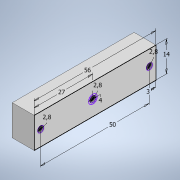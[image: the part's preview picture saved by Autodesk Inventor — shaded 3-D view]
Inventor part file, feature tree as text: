
AUTODESK INVENTOR PART (.ipt)
format: ipt  version: 2020.3 (Build 243373000, 373)  size: 239,616 bytes
history: native  units: mm
features: extrude x2, sketch x1
ambient origin geometry x8: Origin, YZ Plane, XZ Plane, XY Plane, X Axis, Y Axis, Z Axis, Center Point
bodies: Solid1 (feature_tree)
feature tree (3):
  sketch  "Sketch1"  dims[d0=56.0mm d1=14.0mm d2=2.8mm d3=4.0mm d4=27.0mm d5=2.8mm d6=2.8mm d7=50.0mm d8=3.0mm d9=10.0mm d10=0.0mm d11=6.0mm d12=0.0mm]
  extrude  "Extrusion1"  Depth=14.0mm
  extrude  "Extrusion2"  Depth=6.0mm
